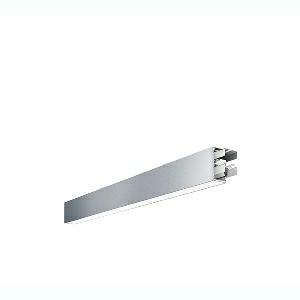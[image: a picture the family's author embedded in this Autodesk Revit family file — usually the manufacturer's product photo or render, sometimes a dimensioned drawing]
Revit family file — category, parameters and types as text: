
# Revit family: dotoo_line_-_dla_1500_830_d_sta_00807964_68c1
name_source: partatom
category: Lighting Fixtures
units: mm (PartAtom-declared; Revit-internal decimal feet)

## family parameters
Cut with Voids When Loaded = No
Host = Face
Light Source = No
Part Type = Normal
Room Calculation Point = No
Round Connector Dimension = Use Diameter
Shared = No

## types (1)
- DOTOO.line - DLA 1500/830/D STA (1 x LED, 1300 lm, 3000K)
    Apparent Load = 13 VA
    Approval mark = CE
    CIE Flux Codes = 67 91 98 100 100
    Color Rendering = 80-89
    Color Temperature = 3000K
    Control Gear = Electronic ballast
    Default Elevation = 1800 mm
    Description = DLA 1500/830/D|Surface-mounted luminaire.|light source: LED|work equipment: Adjustable electronic ballast, digital DALI|connected load: 220-240 V, 50/60 Hz|Power consumption: approx. 13 W|luminous flux: 1300 lm|luminous efficacy: 100 lm/W|light distribution: Direct|colour temperature: Warm white, ca. 3000 K|class of protection: I|technology: Continuously dimmable|mains lead: Connector|glare control: Prism aperture|special features: DALI Load 1x, TouchDIM - dimming via standard switch, Through-wired, up to 18 m on one mains connection, Flicker-free, Suitable as emergency lighting, Start luminaire with mains connection, Mechanical and electrical connection of the individual modules without tools|
    Frequency = 50 Hz
    Height = 110 mm
    Lamp = 1 x LED
    Lamp Light Flux = 1300 lm
    Lamp count = 1
    Length = 1128 mm
    Luminous efficacy = 100 lm/W
    Manufacturer = Waldmann
    ModVariant = No
    Model = 00807964
    Mounting Place = Ceiling
    Mounting Type = Surface mounted
    Number of Poles = 1
    OnlyDefault = Yes
    Power Factor = 1
    Product Name = DOTOO.line - DLA 1500/830/D STA
    Product group = Ceiling mounted luminaire
    ProductGroupID = 3
    Protection Class = Protection class I
    Protection Degree = IP 40
    RLX_Detail_Level = 1
    RLX_Emergency_Light_Flux = 0 lm
    RLX_Emergency_Type = 0
    RLX_Emergency_Type_DB = No
    RlxData = <blob elided: 18365 chars, md5=417a36c6>
    Socket = socket
    Standby Power = 0 W
    System Light Flux = 1300 lm
    System Power = 13 W
    Type Comments = Product without accessories
    Type Image = 114372000-00807949.jpg
    URL = http://relux.com
    VarID = ---
    Voltage = 230 V
    Voltage Range = 220-240 V
    Weight = 0.00 kg
    Width = 60 mm  [stored 0.19685 ft]

note: [stored X ft] marks values corroborated as IEEE doubles in the binary element streams (Revit-internal decimal feet)

## geometry (parser evidence)
native form markers: Blend x4, Sweep x12
no freeform markers — native parametric forms only
